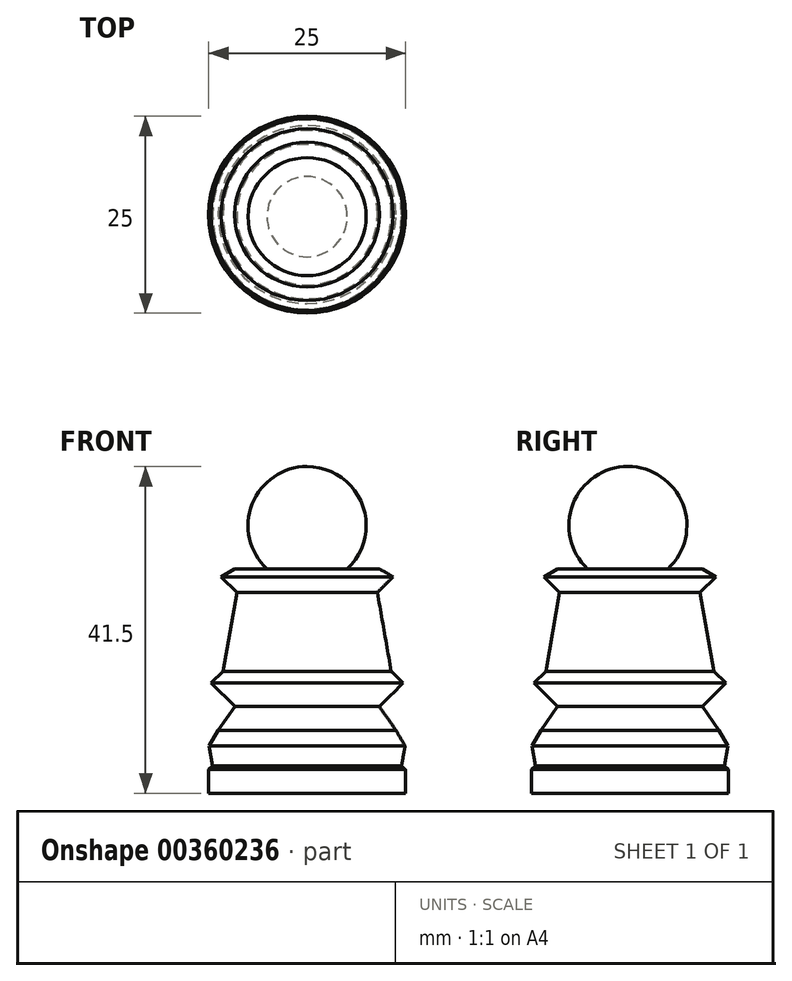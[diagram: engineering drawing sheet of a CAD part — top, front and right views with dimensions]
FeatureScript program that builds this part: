
annotation { "Feature Type Name" : "Feature", "Feature Type Description" : "" }
export const myFeature = defineFeature(function(context is Context, id is Id, definition is map)
    precondition{}
    {
        {
            var Q0;
            Q0=qCreatedBy(makeId("Top.planeOp"),FACE);
            var sketch = newSketch(context, id + "F0", { "sketchPlane" : qUnion([Q0])});
            skCircle(sketch, "E0", {"center": v(0, 0.26) * mm, "radius": 12.5 * mm});
            skSolve(sketch);
        }
        {
            var Q0;
            Q0=makeQuery(id+"F0.imprint","IMPRINT",FACE,{"disambiguationData":[TD([[makeQuery(id+"F0.imprint","IMPRINT",EDGE,{"derivedFrom":sQuery(id+"F0.wireOp",EDGE,"E0")}),1.0]])]});
            extrude(context, id + "F1", {"entities" : qUnion([Q0]), "depth" : 3 * mm});
        }
        {
            var Q0;
            Q0=makeQuery(id+"F1.opExtrude","CAP_FACE",FACE,{"disambiguationData":[OSD([sQuery(id+"F0.wireOp",EDGE,"E0")])],"isStart":false});
            extrude(context, id + "F2", {"entities" : qUnion([Q0]), "operationType" : NewBodyOperationType.ADD, "depth" : 0.5 * mm, "hasDraft" : true, "draftAngle" : 45 * degree, "draftPullDirection" : true});
        }
        {
            var Q0;
            Q0=makeQuery(id+"F2.opExtrude","CAP_FACE",FACE,{"disambiguationData":[OSD([sQuery(id+"F0.wireOp",EDGE,"E0")])],"isStart":false});
            extrude(context, id + "F3", {"entities" : qUnion([Q0]), "operationType" : NewBodyOperationType.ADD, "depth" : 2.5 * mm, "hasDraft" : true, "draftAngle" : 10 * degree});
        }
        {
            var Q0;
            Q0=makeQuery(id+"F3.opExtrude","CAP_FACE",FACE,{"disambiguationData":[OSD([sQuery(id+"F0.wireOp",EDGE,"E0")])],"isStart":false});
            extrude(context, id + "F4", {"entities" : qUnion([Q0]), "operationType" : NewBodyOperationType.ADD, "depth" : 2 * mm, "hasDraft" : true, "draftAngle" : 30 * degree, "draftPullDirection" : true});
        }
        {
            var Q0;
            Q0=makeQuery(id+"F4.opExtrude","CAP_FACE",FACE,{"disambiguationData":[OSD([sQuery(id+"F0.wireOp",EDGE,"E0")])],"isStart":false});
            extrude(context, id + "F5", {"entities" : qUnion([Q0]), "operationType" : NewBodyOperationType.ADD, "depth" : 3 * mm, "hasDraft" : true, "draftAngle" : 35 * degree, "draftPullDirection" : true});
        }
        {
            var Q0;
            Q0=makeQuery(id+"F5.opExtrude","CAP_FACE",FACE,{"disambiguationData":[OSD([sQuery(id+"F0.wireOp",EDGE,"E0")])],"isStart":false});
            extrude(context, id + "F6", {"entities" : qUnion([Q0]), "operationType" : NewBodyOperationType.ADD, "depth" : 1.5 * mm, "hasDraft" : true, "draftAngle" : 45 * degree});
        }
        {
            var Q0;
            Q0=makeQuery(id+"F6.opExtrude","CAP_FACE",FACE,{"disambiguationData":[OSD([sQuery(id+"F0.wireOp",EDGE,"E0")])],"isStart":false});
            extrude(context, id + "F7", {"entities" : qUnion([Q0]), "operationType" : NewBodyOperationType.ADD, "depth" : 1.5 * mm, "hasDraft" : true, "draftAngle" : 45 * degree});
        }
        {
            var Q0;
            Q0=makeQuery(id+"F7.opExtrude","CAP_FACE",FACE,{"disambiguationData":[OSD([sQuery(id+"F0.wireOp",EDGE,"E0")])],"isStart":false});
            extrude(context, id + "F8", {"entities" : qUnion([Q0]), "operationType" : NewBodyOperationType.ADD, "depth" : 1.5 * mm, "hasDraft" : true, "draftAngle" : 45 * degree, "draftPullDirection" : true});
        }
        {
            var Q0;
            Q0=makeQuery(id+"F8.opExtrude","CAP_FACE",FACE,{"disambiguationData":[OSD([sQuery(id+"F0.wireOp",EDGE,"E0")])],"isStart":false});
            extrude(context, id + "F9", {"entities" : qUnion([Q0]), "operationType" : NewBodyOperationType.ADD, "depth" : 10 * mm, "hasDraft" : true, "draftAngle" : 10 * degree, "draftPullDirection" : true});
        }
        {
            var Q0;
            Q0=makeQuery(id+"F9.opExtrude","CAP_FACE",FACE,{"disambiguationData":[OSD([sQuery(id+"F0.wireOp",EDGE,"E0")])],"isStart":false});
            extrude(context, id + "F10", {"entities" : qUnion([Q0]), "operationType" : NewBodyOperationType.ADD, "depth" : 2 * mm, "hasDraft" : true, "draftAngle" : 45 * degree});
        }
        {
            var Q0;
            Q0=makeQuery(id+"F10.opExtrude","CAP_FACE",FACE,{"disambiguationData":[OSD([sQuery(id+"F0.wireOp",EDGE,"E0")])],"isStart":false});
            extrude(context, id + "F11", {"entities" : qUnion([Q0]), "operationType" : NewBodyOperationType.ADD, "depth" : 1 * mm, "hasDraft" : true, "draftAngle" : 60 * degree, "draftPullDirection" : true});
        }
        {
            var Q0;
            Q0=qCreatedBy(makeId("Front.planeOp"),FACE);
            var sketch = newSketch(context, id + "F12", { "sketchPlane" : qUnion([Q0])});
            skLineSegment(sketch, "E1", {"start": v(0, 0) * mm, "end": v(0, 70.48) * mm});
            skCircle(sketch, "E2", {"center": v(0, 34) * mm, "radius": 7.5 * mm});
            skSolve(sketch);
        }
        {
            var Q0;
            {var subQ0=sQuery(id+"F12.wireOp",EDGE,"E2");var subQ1=sQuery(id+"F12.wireOp",EDGE,"E1");var subQ2=makeQuery(id+"F12.imprint","INTERSECT",VERTEX,{"disambiguationData":[OD(0.0)],"derivedFrom":[subQ1,subQ0]});Q0=makeQuery(id+"F12.imprint","IMPRINT",FACE,{"disambiguationData":[TD([[makeQuery(id+"F12.imprint","IMPRINT",EDGE,{"disambiguationData":[TD([[subQ2,-1.0]])],"derivedFrom":subQ1}),1.0]])]});}
            var Q1;
            Q1=sQuery(id+"F12.wireOp",EDGE,"E1");
            revolve(context, id + "F13", {"operationType" : NewBodyOperationType.ADD, "entities" : qUnion([Q0]), "axis" : qUnion([Q1]), "revolveType" : RevolveType.FULL});
        }
    });
